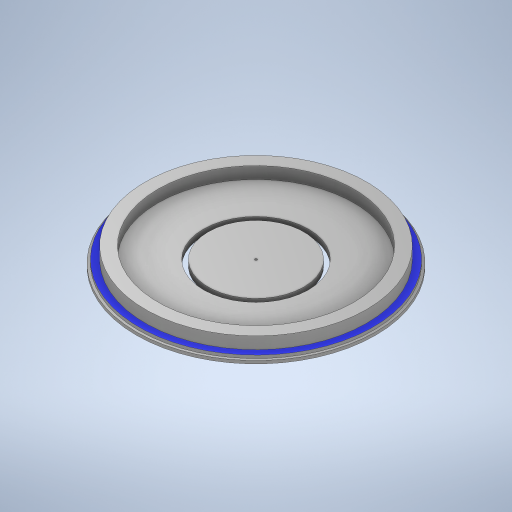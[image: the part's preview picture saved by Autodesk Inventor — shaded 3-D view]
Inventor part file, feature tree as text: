
AUTODESK INVENTOR PART (.ipt)
format: ipt  version: 2024 (Build 280153000, 153)  size: 445,440 bytes
history: native  units: mm
features: extrude x6, sketch x5, revolve x1
ambient origin geometry x8: Origin, YZ Plane, XZ Plane, XY Plane, X Axis, Y Axis, Z Axis, Center Point
bodies: Solid1 (feature_tree)
feature tree (12):
  extrude  "Extrusion1"  Depth=5.0mm TaperAngle=0.0deg
  sketch  "Sketch8"  dims[d17=2.0mm d18=2.0mm]
  extrude  "Extrusion4"  Depth=2.0mm
  revolve  "Revolution2"  Angle=360.0deg
  extrude  "Extrusion5"  Depth=185.0mm
  extrude  "Extrusion6"  Depth=10.0mm
  extrude  "Extrusion7"  Depth=10.0mm
  extrude  "Extrusion8"  TaperAngle=90.0deg  [1 undecoded]
  sketch  "Sketch1"  dims[d0=200.0mm d1=5.0mm d2=0.0mm]
  sketch  "Sketch9"  dims[d19=42.0mm d20=30.0mm d22=360.0deg]
  sketch  "Sketch10"  dims[d27=700.0mm d29=360.0deg d31=185.0mm]
  sketch  "Sketch11"  dims[d32=10.0mm d33=0.0mm d34=2.0mm d35=10.0mm d36=90.0deg d37=164.0mm d38=5.0mm d39=0.0mm d40=180.0mm d41=170.0mm d42=5.0mm d43=0.0mm d44=10.0mm d45=0.0mm d46=88.0mm d47=80.0mm d48=10.0mm d49=0.0mm]
note: 1 required parameter value undecoded (feature->parameter linkage not recoverable at this tier; creation-order binding heuristic only, values carry confidence <= 0.55)
